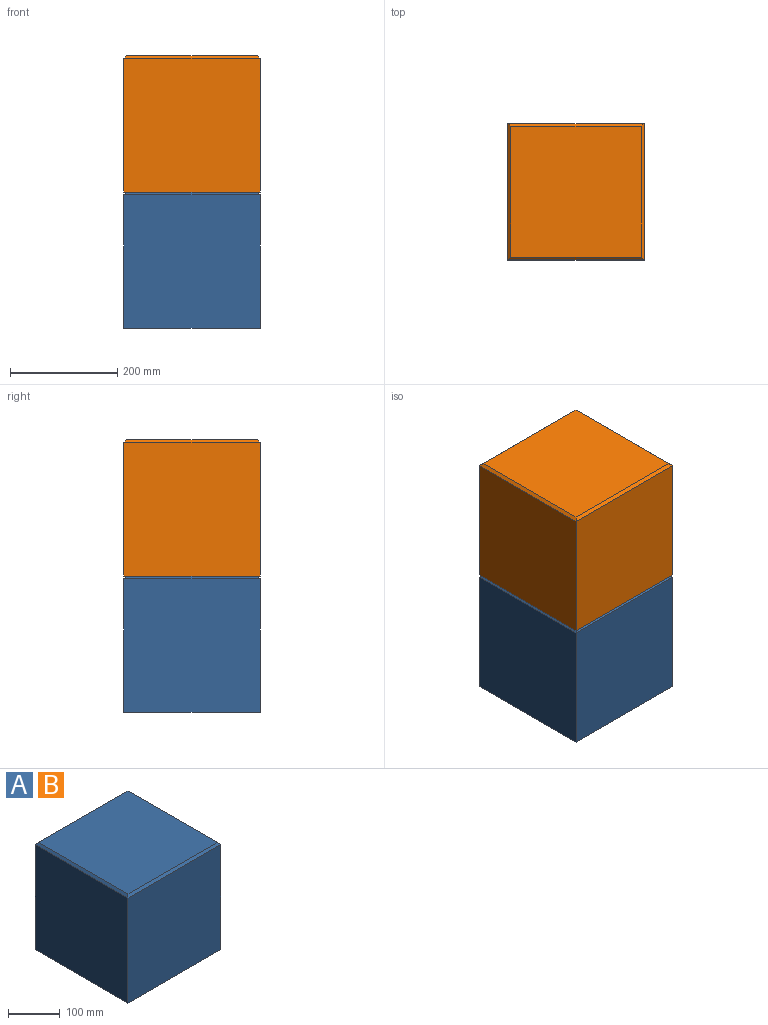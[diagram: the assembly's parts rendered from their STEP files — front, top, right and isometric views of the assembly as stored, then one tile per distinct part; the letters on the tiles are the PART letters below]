
ASSEMBLY  parts=2 mates=1
PART A: 10 faces, bbox 254x254x254 mm
  f0: plane 254x248.92mm, normal (1,0,0), area 63225.7mm2, adj f1,f3,f5,f6
  f1: plane 254x248.92mm, normal (0,1,0), area 63225.7mm2, adj f0,f2,f5,f7
  f2: plane 254x248.92mm, normal (-1,0,0), area 63225.7mm2, adj f1,f3,f5,f9
  f3: plane 254x248.92mm, normal (0,-1,0), area 63225.7mm2, adj f0,f2,f5,f8
  f4: plane 243.84x243.84mm, normal (0,0,1), area 59457.9mm2, adj f6,f7,f8,f9
  f5: plane 254x254mm, normal (0,0,-1), area 64516mm2, adj f0,f1,f2,f3
  f6: plane 254x5.08mm, normal (0.71,0,0.71), area 1788.3mm2, adj f0,f4,f7,f8
  f7: plane 254x5.08mm, normal (0,0.71,0.71), area 1788.3mm2, adj f1,f4,f6,f9
  f8: plane 254x5.08mm, normal (0,-0.71,0.71), area 1788.3mm2, adj f3,f4,f6,f9
  f9: plane 254x5.08mm, normal (-0.71,0,0.71), area 1788.3mm2, adj f2,f4,f7,f8
PART B: same geometry as A
PLACE A t=(-109.98,-15.34,-54.77)mm
PLACE B t=(-109.98,-15.34,199.23)mm
MATE planar B.f5 <-> A.f4  axis (0,0,-1) through (-109.98,-15.34,199.23)mm
